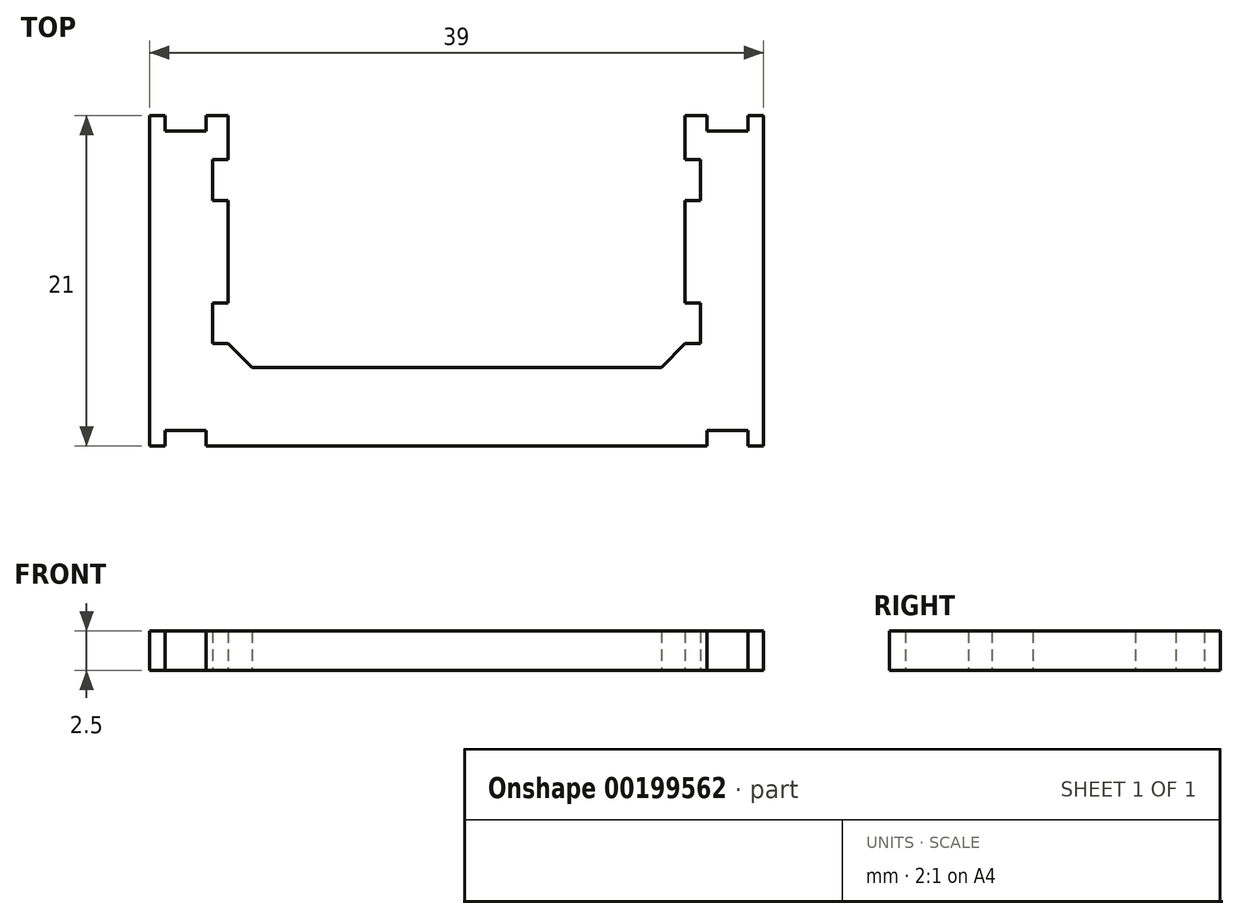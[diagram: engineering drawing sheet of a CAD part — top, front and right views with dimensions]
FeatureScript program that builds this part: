
annotation { "Feature Type Name" : "Feature", "Feature Type Description" : "" }
export const myFeature = defineFeature(function(context is Context, id is Id, definition is map)
    precondition{}
    {
        {
            var Q0;
            Q0=qCreatedBy(makeId("Top.planeOp"),FACE);
            var sketch = newSketch(context, id + "F0", { "sketchPlane" : qUnion([Q0])});
            skLineSegment(sketch, "E0.bottom", {"start": v(19.5, -10.5) * mm, "end": v(18.5, -10.5) * mm});
            skLineSegment(sketch, "E0.top", {"start": v(19.5, 10.5) * mm, "end": v(18.5, 10.5) * mm});
            skLineSegment(sketch, "E0.left", {"start": v(19.5, -10.5) * mm, "end": v(19.5, 10.5) * mm});
            skLineSegment(sketch, "E0.right", {"start": v(-19.5, -10.5) * mm, "end": v(-19.5, 10.5) * mm});
            skPoint(sketch, "E0.middle", {"position": v(0, 0) * mm});
            skLineSegment(sketch, "E1", {"start": v(-14.5, 5.1) * mm, "end": v(-14.5, -1.4) * mm});
            skLineSegment(sketch, "E2", {"start": v(-18.5, 9.5) * mm, "end": v(-15.9, 9.5) * mm});
            skLineSegment(sketch, "E3", {"start": v(-18.5, -9.5) * mm, "end": v(-15.9, -9.5) * mm});
            skLineSegment(sketch, "E4", {"start": v(-18.5, 10.5) * mm, "end": v(-18.5, 9.5) * mm});
            skLineSegment(sketch, "E5", {"start": v(18.5, 10.5) * mm, "end": v(18.5, 9.5) * mm});
            skLineSegment(sketch, "E6", {"start": v(-15.9, 10.5) * mm, "end": v(-15.9, 9.5) * mm});
            skLineSegment(sketch, "E7", {"start": v(15.9, 10.5) * mm, "end": v(15.9, 9.5) * mm});
            skLineSegment(sketch, "E8", {"start": v(-13, -5.5) * mm, "end": v(13, -5.5) * mm});
            skLineSegment(sketch, "E9", {"start": v(-15.5, 7.7) * mm, "end": v(-15.5, 5.1) * mm});
            skLineSegment(sketch, "E10", {"start": v(15.5, 7.7) * mm, "end": v(15.5, 5.1) * mm});
            skLineSegment(sketch, "E11", {"start": v(14.5, 5.1) * mm, "end": v(14.5, -1.4) * mm});
            skLineSegment(sketch, "E12", {"start": v(15.5, -4) * mm, "end": v(14.5, -4) * mm});
            skLineSegment(sketch, "E13.trimOffspring", {"start": v(-18.5, -10.5) * mm, "end": v(-19.5, -10.5) * mm});
            skLineSegment(sketch, "E14.trimOffspring", {"start": v(-18.5, -9.5) * mm, "end": v(-18.5, -10.5) * mm});
            skLineSegment(sketch, "E15.trimOffspring", {"start": v(-15.9, -9.5) * mm, "end": v(-15.9, -10.5) * mm});
            skLineSegment(sketch, "E16.trimOffspring", {"start": v(15.9, -9.5) * mm, "end": v(18.5, -9.5) * mm});
            skLineSegment(sketch, "E17.trimOffspring", {"start": v(18.5, -9.5) * mm, "end": v(18.5, -10.5) * mm});
            skLineSegment(sketch, "E18.trimOffspring", {"start": v(15.9, -9.5) * mm, "end": v(15.9, -10.5) * mm});
            skLineSegment(sketch, "E19.trimOffspring", {"start": v(15.9, 9.5) * mm, "end": v(18.5, 9.5) * mm});
            skLineSegment(sketch, "E20.trimOffspring", {"start": v(-18.5, 10.5) * mm, "end": v(-19.5, 10.5) * mm});
            skLineSegment(sketch, "E21.trimOffspring", {"start": v(15.9, 10.5) * mm, "end": v(14.5, 10.5) * mm});
            skLineSegment(sketch, "E22.trimOffspring", {"start": v(15.9, -10.5) * mm, "end": v(-15.9, -10.5) * mm});
            skLineSegment(sketch, "E23", {"start": v(-15.5, 7.7) * mm, "end": v(-14.5, 7.7) * mm});
            skLineSegment(sketch, "E24", {"start": v(-15.5, 5.1) * mm, "end": v(-14.5, 5.1) * mm});
            skLineSegment(sketch, "E25", {"start": v(-15.5, -1.4) * mm, "end": v(-14.5, -1.4) * mm});
            skLineSegment(sketch, "E26.trimOffspring", {"start": v(-15.5, -1.4) * mm, "end": v(-15.5, -4) * mm});
            skLineSegment(sketch, "E27.trimOffspring", {"start": v(15.5, -1.4) * mm, "end": v(15.5, -4) * mm});
            skLineSegment(sketch, "E28.trimOffspring", {"start": v(14.5, -1.4) * mm, "end": v(15.5, -1.4) * mm});
            skLineSegment(sketch, "E29.trimOffspring", {"start": v(14.5, 5.1) * mm, "end": v(15.5, 5.1) * mm});
            skLineSegment(sketch, "E30.trimOffspring", {"start": v(-14.5, -4) * mm, "end": v(-15.5, -4) * mm});
            skLineSegment(sketch, "E31", {"start": v(14.5, -4) * mm, "end": v(13, -5.5) * mm});
            skPoint(sketch, "E32", {"position": v(-13, -5.5) * mm});
            skLineSegment(sketch, "E33", {"start": v(-14.5, -4) * mm, "end": v(-13, -5.5) * mm});
            skLineSegment(sketch, "E34", {"start": v(-14.5, 7.7) * mm, "end": v(-14.5, 10.5) * mm});
            skLineSegment(sketch, "E35", {"start": v(14.5, 7.7) * mm, "end": v(14.5, 10.5) * mm});
            skLineSegment(sketch, "E36.trimOffspring", {"start": v(14.5, 7.7) * mm, "end": v(15.5, 7.7) * mm});
            skLineSegment(sketch, "E37.trimOffspring", {"start": v(-14.5, 10.5) * mm, "end": v(-15.9, 10.5) * mm});
            skSolve(sketch);
        }
        {
            var Q0;
            Q0=makeQuery(id+"F0.imprint","IMPRINT",FACE,{"disambiguationData":[TD([[makeQuery(id+"F0.imprint","IMPRINT",EDGE,{"derivedFrom":sQuery(id+"F0.wireOp",EDGE,"E0.bottom")}),-1.0]])]});
            extrude(context, id + "F1", {"entities" : qUnion([Q0]), "depth" : 2.5 * mm});
        }
    });
